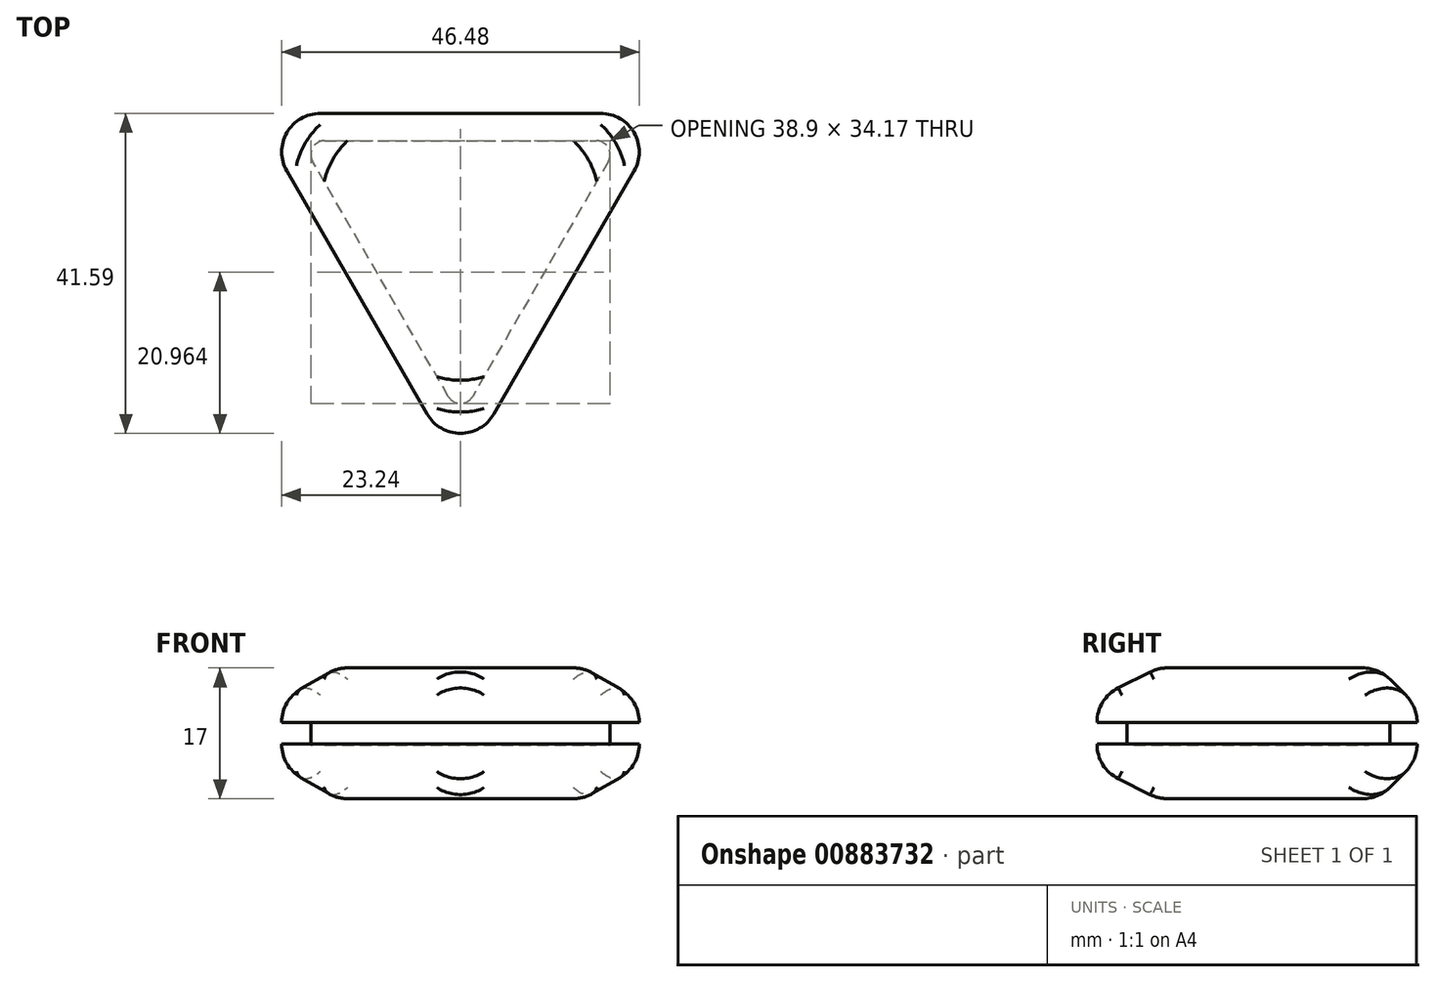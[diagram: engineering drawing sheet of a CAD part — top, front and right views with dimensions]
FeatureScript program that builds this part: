
annotation { "Feature Type Name" : "Feature", "Feature Type Description" : "" }
export const myFeature = defineFeature(function(context is Context, id is Id, definition is map)
    precondition{}
    {
        {
            var Q0;
            Q0=qCreatedBy(makeId("Top.planeOp"),FACE);
            var sketch = newSketch(context, id + "F0", { "sketchPlane" : qUnion([Q0])});
            skCircle(sketch, "E0.cCircle", {"center": v(0, 0) * mm, "radius": 31.06 * mm, "construction": true});
            skLineSegment(sketch, "E0.0", {"start": v(0, -31.06) * mm, "end": v(-26.9, 15.53) * mm});
            skLineSegment(sketch, "E0.1", {"start": v(-26.9, 15.53) * mm, "end": v(26.9, 15.53) * mm});
            skLineSegment(sketch, "E0.2", {"start": v(26.9, 15.53) * mm, "end": v(0, -31.06) * mm});
            skSolve(sketch);
        }
        {
            var Q0;
            Q0=makeQuery(id+"F0.imprint","IMPRINT",FACE,{"disambiguationData":[TD([[makeQuery(id+"F0.imprint","IMPRINT",EDGE,{"derivedFrom":sQuery(id+"F0.wireOp",EDGE,"E0.0")}),-1.0]])]});
            extrude(context, id + "F1", {"entities" : qUnion([Q0]), "depth" : 10 * mm, "offsetDistance" : 25 * mm});
        }
        {
            var Q0;
            Q0=makeQuery(id+"F1.opExtrude","CAP_FACE",FACE,{"disambiguationData":[OSD([sQuery(id+"F0.wireOp",EDGE,"E0.0"),sQuery(id+"F0.wireOp",EDGE,"E0.1"),sQuery(id+"F0.wireOp",EDGE,"E0.2")])],"isStart":true});
            chamfer(context, id + "F2", {"entities" : qUnion([Q0]), "width" : 5 * mm, "tangentPropagation" : true});
        }
        {
            var Q0;
            {var subQ0=sQuery(id+"F0.wireOp",EDGE,"E0.2");Q0=makeQuery(id+"F2.opChamfer","BLEND_EDGE",EDGE,{"blendedFrom":[makeQuery(id+"F1.opExtrude","CAP_EDGE",EDGE,{"disambiguationData":[OSD([subQ0])],"isStart":true}),makeQuery(id+"F1.opExtrude","CAP_FACE",FACE,{"disambiguationData":[OSD([sQuery(id+"F0.wireOp",EDGE,"E0.0"),sQuery(id+"F0.wireOp",EDGE,"E0.1"),subQ0])],"isStart":true})],"blendedInto":[makeQuery(id+"F1.opExtrude","CAP_FACE",FACE,{"disambiguationData":[OSD([sQuery(id+"F0.wireOp",EDGE,"E0.0"),sQuery(id+"F0.wireOp",EDGE,"E0.1"),subQ0])],"isStart":true})]});}
            var Q1;
            {var subQ0=sQuery(id+"F0.wireOp",EDGE,"E0.1");Q1=makeQuery(id+"F2.opChamfer","BLEND_EDGE",EDGE,{"blendedFrom":[makeQuery(id+"F1.opExtrude","CAP_EDGE",EDGE,{"disambiguationData":[OSD([subQ0])],"isStart":true}),makeQuery(id+"F1.opExtrude","CAP_FACE",FACE,{"disambiguationData":[OSD([sQuery(id+"F0.wireOp",EDGE,"E0.0"),subQ0,sQuery(id+"F0.wireOp",EDGE,"E0.2")])],"isStart":true})],"blendedInto":[makeQuery(id+"F1.opExtrude","CAP_FACE",FACE,{"disambiguationData":[OSD([sQuery(id+"F0.wireOp",EDGE,"E0.0"),subQ0,sQuery(id+"F0.wireOp",EDGE,"E0.2")])],"isStart":true})]});}
            var Q2;
            {var subQ0=sQuery(id+"F0.wireOp",EDGE,"E0.0");Q2=makeQuery(id+"F2.opChamfer","BLEND_EDGE",EDGE,{"blendedFrom":[makeQuery(id+"F1.opExtrude","CAP_EDGE",EDGE,{"disambiguationData":[OSD([subQ0])],"isStart":true}),makeQuery(id+"F1.opExtrude","CAP_FACE",FACE,{"disambiguationData":[OSD([subQ0,sQuery(id+"F0.wireOp",EDGE,"E0.1"),sQuery(id+"F0.wireOp",EDGE,"E0.2")])],"isStart":true})],"blendedInto":[makeQuery(id+"F1.opExtrude","CAP_FACE",FACE,{"disambiguationData":[OSD([subQ0,sQuery(id+"F0.wireOp",EDGE,"E0.1"),sQuery(id+"F0.wireOp",EDGE,"E0.2")])],"isStart":true})]});}
            fillet(context, id + "F3", {"entities" : qUnion([Q0, Q1, Q2]), "radius" : 5 * mm, "tangentPropagation" : true, "allowEdgeOverflow" : false});
        }
        {
            var Q0;
            {var subQ0=sQuery(id+"F0.wireOp",EDGE,"E0.0");Q0=makeQuery(id+"F2.opChamfer","BLEND_EDGE",EDGE,{"blendedFrom":[makeQuery(id+"F1.opExtrude","CAP_EDGE",EDGE,{"disambiguationData":[OSD([subQ0])],"isStart":true}),makeQuery(id+"F1.opExtrude","SWEPT_FACE",FACE,{"disambiguationData":[OSD([subQ0])]})],"blendedInto":[makeQuery(id+"F1.opExtrude","SWEPT_FACE",FACE,{"disambiguationData":[OSD([subQ0])]})]});}
            var Q1;
            {var subQ0=sQuery(id+"F0.wireOp",EDGE,"E0.2");Q1=makeQuery(id+"F2.opChamfer","BLEND_EDGE",EDGE,{"blendedFrom":[makeQuery(id+"F1.opExtrude","CAP_EDGE",EDGE,{"disambiguationData":[OSD([subQ0])],"isStart":true}),makeQuery(id+"F1.opExtrude","SWEPT_FACE",FACE,{"disambiguationData":[OSD([subQ0])]})],"blendedInto":[makeQuery(id+"F1.opExtrude","SWEPT_FACE",FACE,{"disambiguationData":[OSD([subQ0])]})]});}
            var Q2;
            {var subQ0=sQuery(id+"F0.wireOp",EDGE,"E0.1");Q2=makeQuery(id+"F2.opChamfer","BLEND_EDGE",EDGE,{"blendedFrom":[makeQuery(id+"F1.opExtrude","CAP_EDGE",EDGE,{"disambiguationData":[OSD([subQ0])],"isStart":true}),makeQuery(id+"F1.opExtrude","SWEPT_FACE",FACE,{"disambiguationData":[OSD([subQ0])]})],"blendedInto":[makeQuery(id+"F1.opExtrude","SWEPT_FACE",FACE,{"disambiguationData":[OSD([subQ0])]})]});}
            fillet(context, id + "F4", {"entities" : qUnion([Q0, Q1, Q2]), "radius" : 5 * mm, "tangentPropagation" : true, "allowEdgeOverflow" : false});
        }
        {
            var Q0;
            Q0=makeQuery(id+"F1.opExtrude","SWEPT_EDGE",EDGE,{"disambiguationData":[OSD([sQuery(id+"F0.wireOp",EDGE,"E0.1"),sQuery(id+"F0.wireOp",EDGE,"E0.2")])]});
            var Q1;
            Q1=makeQuery(id+"F1.opExtrude","SWEPT_EDGE",EDGE,{"disambiguationData":[OSD([sQuery(id+"F0.wireOp",EDGE,"E0.0"),sQuery(id+"F0.wireOp",EDGE,"E0.1")])]});
            var Q2;
            Q2=makeQuery(id+"F1.opExtrude","SWEPT_EDGE",EDGE,{"disambiguationData":[OSD([sQuery(id+"F0.wireOp",EDGE,"E0.0"),sQuery(id+"F0.wireOp",EDGE,"E0.2")])]});
            fillet(context, id + "F5", {"entities" : qUnion([Q0, Q1, Q2]), "radius" : 5 * mm, "tangentPropagation" : true, "allowEdgeOverflow" : false});
        }
        {
            var Q0;
            Q0=makeQuery(id+"F1.opExtrude","CAP_FACE",FACE,{"disambiguationData":[OSD([sQuery(id+"F0.wireOp",EDGE,"E0.0"),sQuery(id+"F0.wireOp",EDGE,"E0.1"),sQuery(id+"F0.wireOp",EDGE,"E0.2")])],"isStart":false});
            cPlane(context, id + "F6", {"entities" : qUnion([Q0]), "cplaneType" : CPlaneType.OFFSET, "offset" : 0 * mm, "width" : 150 * mm, "height" : 150 * mm});
        }
        {
            var Q0;
            Q0=qCreatedBy(id+"F6.planeOp",FACE);
            var sketch = newSketch(context, id + "F7", { "sketchPlane" : qUnion([Q0])});
            skCircle(sketch, "E1.cCircle", {"center": v(0, 0) * mm, "radius": 12 * mm, "construction": true});
            skLineSegment(sketch, "E1.0", {"start": v(-20.77, 12) * mm, "end": v(20.77, 12) * mm});
            skLineSegment(sketch, "E1.1", {"start": v(20.77, 12) * mm, "end": v(0, -23.98) * mm});
            skLineSegment(sketch, "E1.2", {"start": v(0, -23.98) * mm, "end": v(-20.77, 12) * mm});
            skPoint(sketch, "E1.0.midPoint", {"position": v(0, 12) * mm});
            skCircle(sketch, "E2.cCircle", {"center": v(0, 0) * mm, "radius": 22.35 * mm, "construction": true});
            skLineSegment(sketch, "E2.0", {"start": v(-38.72, 22.35) * mm, "end": v(38.72, 22.35) * mm});
            skLineSegment(sketch, "E2.1", {"start": v(38.72, 22.35) * mm, "end": v(0, -44.7) * mm});
            skLineSegment(sketch, "E2.2", {"start": v(0, -44.7) * mm, "end": v(-38.72, 22.35) * mm});
            skPoint(sketch, "E2.0.midPoint", {"position": v(0, 22.35) * mm});
            skSolve(sketch);
        }
        {
            var Q0;
            Q0=makeQuery(id+"F7.imprint","IMPRINT",FACE,{"disambiguationData":[TD([[makeQuery(id+"F7.imprint","IMPRINT",EDGE,{"derivedFrom":sQuery(id+"F7.wireOp",EDGE,"E1.0")}),1.0]])]});
            extrude(context, id + "F8", {"entities" : qUnion([Q0]), "operationType" : NewBodyOperationType.REMOVE, "oppositeDirection" : true, "depth" : 2.9 * mm, "offsetDistance" : 25 * mm});
        }
        {
            var Q0;
            Q0=makeQuery(id+"F8.boolean.opBoolean","COPY",EDGE,{"derivedFrom":makeQuery(id+"F8.opExtrude","SWEPT_EDGE",EDGE,{"disambiguationData":[OSD([sQuery(id+"F7.wireOp",EDGE,"E1.1"),sQuery(id+"F7.wireOp",EDGE,"E1.2")])]})});
            var Q1;
            Q1=makeQuery(id+"F8.boolean.opBoolean","COPY",EDGE,{"derivedFrom":makeQuery(id+"F8.opExtrude","SWEPT_EDGE",EDGE,{"disambiguationData":[OSD([sQuery(id+"F7.wireOp",EDGE,"E1.0"),sQuery(id+"F7.wireOp",EDGE,"E1.2")])]})});
            var Q2;
            Q2=makeQuery(id+"F8.boolean.opBoolean","COPY",EDGE,{"derivedFrom":makeQuery(id+"F8.opExtrude","SWEPT_EDGE",EDGE,{"disambiguationData":[OSD([sQuery(id+"F7.wireOp",EDGE,"E1.0"),sQuery(id+"F7.wireOp",EDGE,"E1.1")])]})});
            fillet(context, id + "F9", {"entities" : qUnion([Q0, Q1, Q2]), "radius" : 1.8 * mm, "tangentPropagation" : true, "allowEdgeOverflow" : false});
        }
        {
            var Q0;
            Q0=makeQuery(id+"F1.opExtrude","SWEPT_BODY",BODY,{"disambiguationData":[OSD([sQuery(id+"F0.wireOp",EDGE,"E0.0"),sQuery(id+"F0.wireOp",EDGE,"E0.1"),sQuery(id+"F0.wireOp",EDGE,"E0.2")])]});
            var Q1;
            Q1=makeQuery(id+"F1.opExtrude","CAP_FACE",FACE,{"disambiguationData":[OSD([sQuery(id+"F0.wireOp",EDGE,"E0.0"),sQuery(id+"F0.wireOp",EDGE,"E0.1"),sQuery(id+"F0.wireOp",EDGE,"E0.2")])],"isStart":false});
            mirror(context, id + "F10", {"entities" : qUnion([Q0]), "mirrorPlane" : qUnion([Q1])});
        }
        {
            var Q0;
            Q0=makeQuery(id+"F10.opPattern","COPY",BODY,{"derivedFrom":makeQuery(id+"F1.opExtrude","SWEPT_BODY",BODY,{"disambiguationData":[OSD([sQuery(id+"F0.wireOp",EDGE,"E0.0"),sQuery(id+"F0.wireOp",EDGE,"E0.1"),sQuery(id+"F0.wireOp",EDGE,"E0.2")])]}),"instanceName":"1"});
            transform(context, id + "F11", {"entities" : qUnion([Q0]), "transformType" : TransformType.TRANSLATION_3D, "dx" : 0 * mm, "dy" : 0 * mm, "dz" : -3 * mm, "makeCopy" : false});
        }
    });
